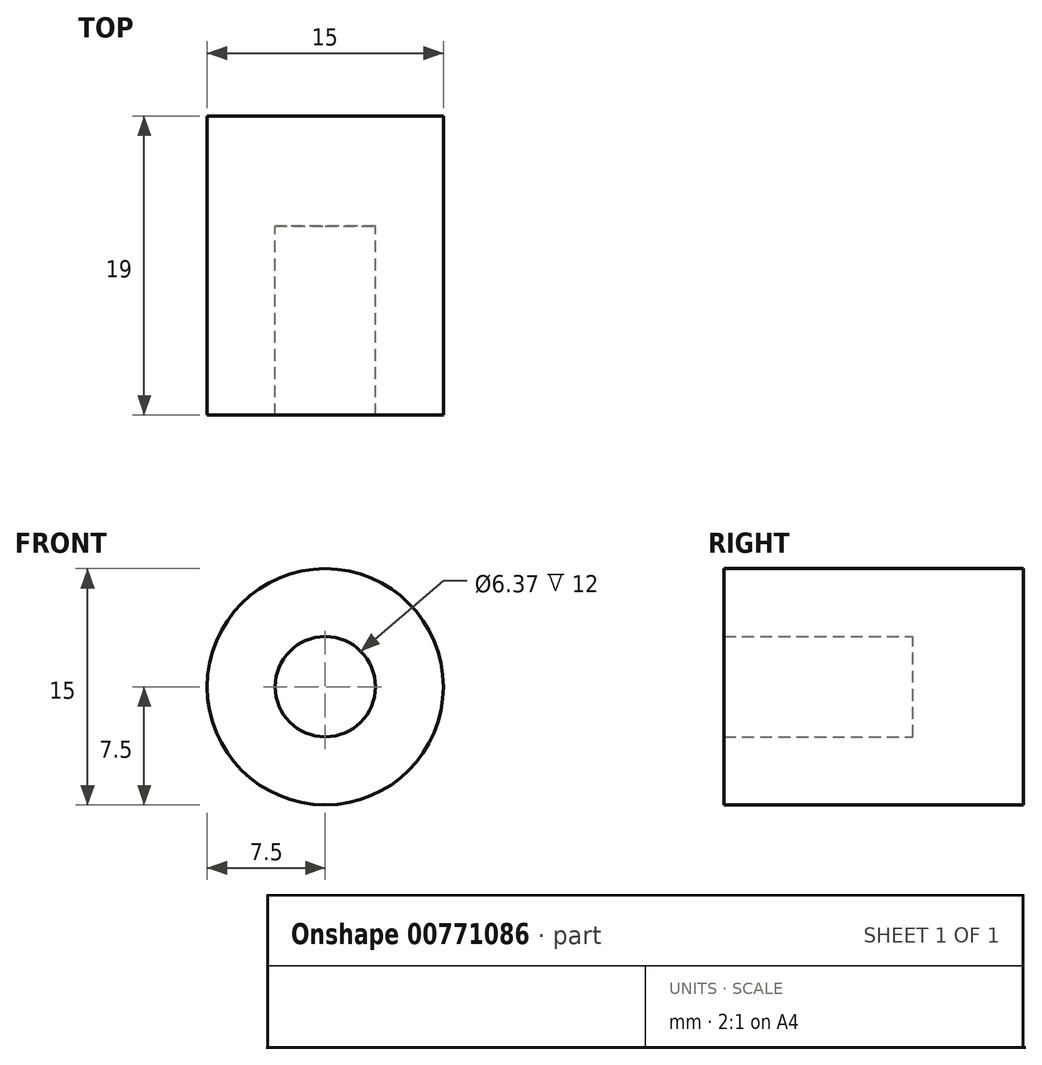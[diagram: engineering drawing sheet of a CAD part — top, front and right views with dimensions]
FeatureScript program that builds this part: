
annotation { "Feature Type Name" : "Feature", "Feature Type Description" : "" }
export const myFeature = defineFeature(function(context is Context, id is Id, definition is map)
    precondition{}
    {
        {
            var Q0;
            Q0=qCreatedBy(makeId("Front.planeOp"),FACE);
            var sketch = newSketch(context, id + "F0", { "sketchPlane" : qUnion([Q0])});
            skCircle(sketch, "E0", {"center": v(0, 0) * mm, "radius": 7.5 * mm});
            skCircle(sketch, "E1", {"center": v(0, 0) * mm, "radius": 3.19 * mm});
            skSolve(sketch);
        }
        {
            var Q0;
            Q0 = qSketchRegion(id + "F0", true);
            extrude(context, id + "F1", {"entities" : qUnion([Q0]), "depth" : 12 * mm, "offsetDistance" : 25 * mm});
        }
        {
            var Q0;
            Q0=makeQuery(id+"F1.opExtrude","CAP_FACE",FACE,{"disambiguationData":[OSD([sQuery(id+"F0.wireOp",EDGE,"E0"),sQuery(id+"F0.wireOp",EDGE,"E1")])],"isStart":true});
            var sketch = newSketch(context, id + "F2", { "sketchPlane" : qUnion([Q0])});
            skSolve(sketch);
        }
        {
            var Q0;
            Q0 = qSketchRegion(id + "F2", true);
            var Q1;
            Q1=makeQuery(id+"F2.imprint","IMPRINT",FACE,{"disambiguationData":[TD([[makeQuery(id+"F2.imprint","IMPRINT",EDGE,{"derivedFrom":makeQuery(id+"F1.opExtrude","CAP_EDGE",EDGE,{"disambiguationData":[OSD([sQuery(id+"F0.wireOp",EDGE,"E1")])],"isStart":true})}),-1.0]])]});
            var Q2;
            Q2=makeQuery(id+"F2.imprint","IMPRINT",FACE,{"disambiguationData":[TD([[makeQuery(id+"F2.imprint","IMPRINT",EDGE,{"derivedFrom":makeQuery(id+"F1.opExtrude","CAP_EDGE",EDGE,{"disambiguationData":[OSD([sQuery(id+"F0.wireOp",EDGE,"E0")])],"isStart":true})}),-1.0]])]});
            extrude(context, id + "F3", {"entities" : qUnion([Q0, Q1, Q2]), "operationType" : NewBodyOperationType.ADD, "depth" : 7 * mm, "offsetDistance" : 25 * mm});
        }
    });
